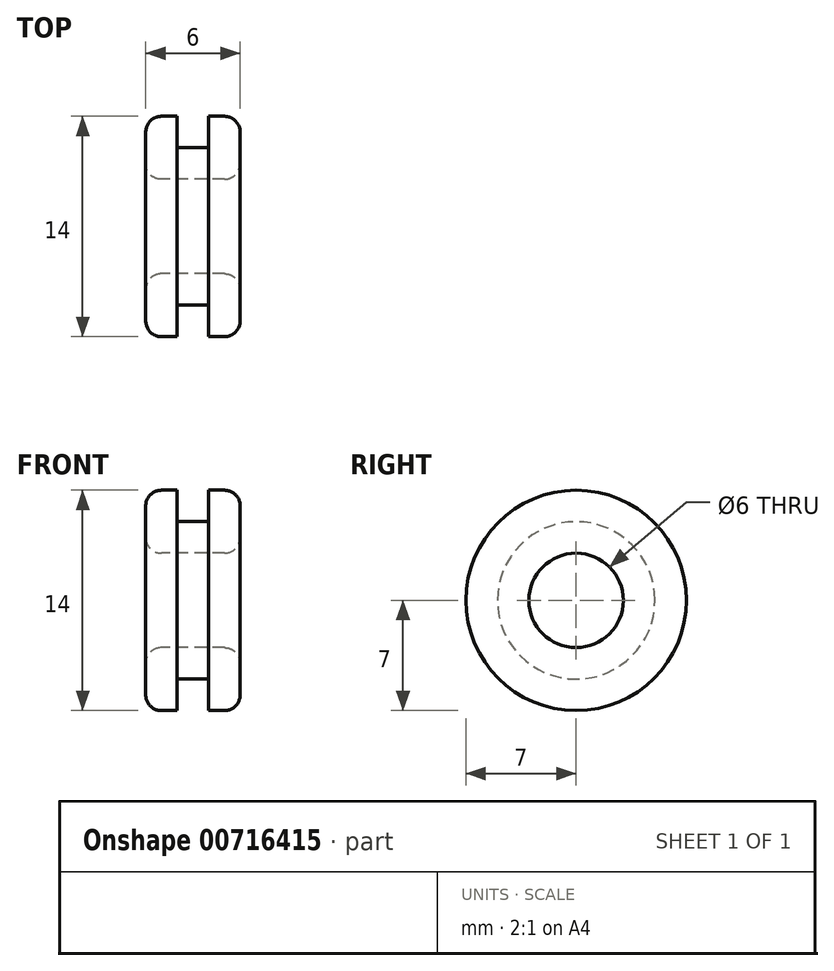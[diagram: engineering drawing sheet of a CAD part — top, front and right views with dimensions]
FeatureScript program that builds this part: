
annotation { "Feature Type Name" : "Feature", "Feature Type Description" : "" }
export const myFeature = defineFeature(function(context is Context, id is Id, definition is map)
    precondition{}
    {
        {
            var Q0;
            Q0=qCreatedBy(makeId("Top.planeOp"),FACE);
            var sketch = newSketch(context, id + "F0", { "sketchPlane" : qUnion([Q0])});
            skLineSegment(sketch, "E0", {"start": v(-5.48, 0) * mm, "end": v(9.24, 0) * mm, "construction": true});
            skLineSegment(sketch, "E1", {"start": v(-3, -3) * mm, "end": v(0, -3) * mm});
            skLineSegment(sketch, "E2", {"start": v(0, -3) * mm, "end": v(3, -3) * mm});
            skLineSegment(sketch, "E3", {"start": v(-3, -3) * mm, "end": v(-3, -6) * mm});
            skLineSegment(sketch, "E4", {"start": v(3, -3) * mm, "end": v(3, -6) * mm});
            skLineSegment(sketch, "E5", {"start": v(0, -5) * mm, "end": v(-1, -5) * mm});
            skLineSegment(sketch, "E6", {"start": v(0, -5) * mm, "end": v(1, -5) * mm});
            skLineSegment(sketch, "E7", {"start": v(-1, -5) * mm, "end": v(-1, -7) * mm});
            skLineSegment(sketch, "E8", {"start": v(1, -5) * mm, "end": v(1, -7) * mm});
            skPoint(sketch, "E9.orphan", {"position": v(-3, -6) * mm});
            skLineSegment(sketch, "E10", {"start": v(-1, -7) * mm, "end": v(-2, -7) * mm});
            skArc(sketch, "E11", {"start": v(-3, -6) * mm, "mid": v(-2.7, -6.7) * mm, "end": v(-2, -7) * mm});
            skLineSegment(sketch, "E12", {"start": v(1, -7) * mm, "end": v(2, -7) * mm});
            skArc(sketch, "E13", {"start": v(2, -7) * mm, "mid": v(2.7, -6.7) * mm, "end": v(3, -6) * mm});
            skSolve(sketch);
        }
        {
            var Q0;
            Q0 = qSketchRegion(id + "F0", true);
            var Q1;
            Q1=sQuery(id+"F0.wireOp",EDGE,"E0");
            revolve(context, id + "F1", {"surfaceOperationType" : NewSurfaceOperationType.NEW, "entities" : qUnion([Q0]), "axis" : qUnion([Q1]), "revolveType" : RevolveType.FULL});
        }
        {
            var Q0;
            Q0=makeQuery(id+"F1.opRevolve","SWEPT_EDGE",EDGE,{"disambiguationData":[OSD([sQuery(id+"F0.wireOp",EDGE,"E1"),sQuery(id+"F0.wireOp",EDGE,"E3")])]});
            var Q1;
            Q1=makeQuery(id+"F1.opRevolve","SWEPT_EDGE",EDGE,{"disambiguationData":[OSD([sQuery(id+"F0.wireOp",EDGE,"E2"),sQuery(id+"F0.wireOp",EDGE,"E4")])]});
            fillet(context, id + "F2", {"entities" : qUnion([Q0, Q1]), "radius" : 1 * mm, "tangentPropagation" : true, "allowEdgeOverflow" : false});
        }
    });
